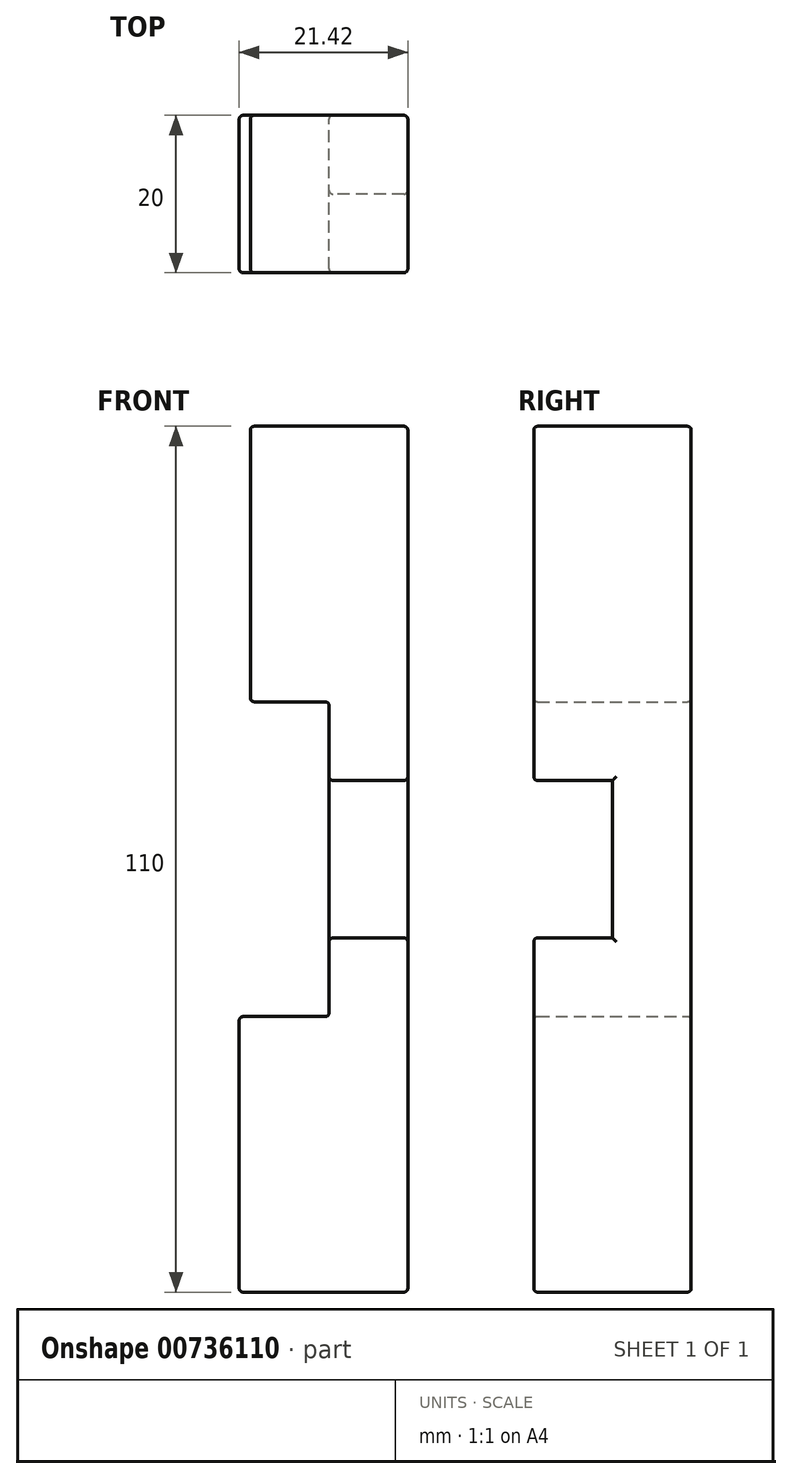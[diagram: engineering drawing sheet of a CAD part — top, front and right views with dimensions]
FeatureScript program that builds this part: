
annotation { "Feature Type Name" : "Feature", "Feature Type Description" : "" }
export const myFeature = defineFeature(function(context is Context, id is Id, definition is map)
    precondition{}
    {
        {
            var Q0;
            Q0=qCreatedBy(makeId("Front.planeOp"),FACE);
            var sketch = newSketch(context, id + "F0", { "sketchPlane" : qUnion([Q0])});
            skLineSegment(sketch, "E0", {"start": v(-10, 21.51) * mm, "end": v(-10, 56.51) * mm});
            skLineSegment(sketch, "E1", {"start": v(-10, 56.51) * mm, "end": v(10, 56.51) * mm});
            skLineSegment(sketch, "E2", {"start": v(10, 56.51) * mm, "end": v(10, -53.49) * mm});
            skLineSegment(sketch, "E3", {"start": v(10, -53.49) * mm, "end": v(-11.42, -53.49) * mm});
            skLineSegment(sketch, "E4", {"start": v(-11.42, -53.49) * mm, "end": v(-11.42, -18.49) * mm});
            skLineSegment(sketch, "E5", {"start": v(-11.42, -18.49) * mm, "end": v(0, -18.49) * mm});
            skLineSegment(sketch, "E6", {"start": v(0, -18.49) * mm, "end": v(0, 21.51) * mm});
            skLineSegment(sketch, "E7", {"start": v(0, 21.51) * mm, "end": v(-10, 21.51) * mm});
            skLineSegment(sketch, "E8", {"start": v(0, 11.51) * mm, "end": v(10, 11.51) * mm});
            skLineSegment(sketch, "E9", {"start": v(0, -8.49) * mm, "end": v(10, -8.49) * mm});
            skSolve(sketch);
        }
        {
            var Q0;
            Q0=makeQuery(id+"F0.imprint","IMPRINT",FACE,{"disambiguationData":[TD([[makeQuery(id+"F0.imprint","IMPRINT",EDGE,{"derivedFrom":sQuery(id+"F0.wireOp",EDGE,"E0")}),-1.0]])]});
            var Q1;
            {var subQ1=sQuery(id+"F0.wireOp",EDGE,"E3");Q1=makeQuery(id+"F0.imprint","IMPRINT",FACE,{"disambiguationData":[TD([[makeQuery(id+"F0.imprint","IMPRINT",EDGE,{"derivedFrom":subQ1}),-1.0]])]});}
            var Q2;
            {var subQ0=sQuery(id+"F0.wireOp",EDGE,"E8");Q2=makeQuery(id+"F0.imprint","IMPRINT",FACE,{"disambiguationData":[TD([[makeQuery(id+"F0.imprint","IMPRINT",EDGE,{"derivedFrom":subQ0}),-1.0]])]});}
            extrude(context, id + "F1", {"entities" : qUnion([Q0, Q1, Q2]), "depth" : 10 * mm, "offsetDistance" : 25 * mm});
        }
        {
            var Q0;
            Q0=makeQuery(id+"F0.imprint","IMPRINT",FACE,{"disambiguationData":[TD([[makeQuery(id+"F0.imprint","IMPRINT",EDGE,{"derivedFrom":sQuery(id+"F0.wireOp",EDGE,"E0")}),-1.0]])]});
            var Q1;
            {var subQ1=sQuery(id+"F0.wireOp",EDGE,"E3");Q1=makeQuery(id+"F0.imprint","IMPRINT",FACE,{"disambiguationData":[TD([[makeQuery(id+"F0.imprint","IMPRINT",EDGE,{"derivedFrom":subQ1}),-1.0]])]});}
            extrude(context, id + "F2", {"entities" : qUnion([Q0, Q1]), "operationType" : NewBodyOperationType.ADD, "depth" : 20 * mm, "offsetDistance" : 25 * mm});
        }
        {
            var Q0;
            Q0=makeQuery(id+"F2.opExtrude","CAP_FACE",FACE,{"disambiguationData":[OSD([sQuery(id+"F0.wireOp",EDGE,"E0"),sQuery(id+"F0.wireOp",EDGE,"E1"),sQuery(id+"F0.wireOp",EDGE,"E2"),sQuery(id+"F0.wireOp",EDGE,"E6"),sQuery(id+"F0.wireOp",EDGE,"E7"),sQuery(id+"F0.wireOp",EDGE,"E8")])],"isStart":false});
            var Q1;
            Q1=makeQuery(id+"F2.opExtrude","CAP_FACE",FACE,{"disambiguationData":[OSD([sQuery(id+"F0.wireOp",EDGE,"E2"),sQuery(id+"F0.wireOp",EDGE,"E3"),sQuery(id+"F0.wireOp",EDGE,"E4"),sQuery(id+"F0.wireOp",EDGE,"E5"),sQuery(id+"F0.wireOp",EDGE,"E6"),sQuery(id+"F0.wireOp",EDGE,"E9")])],"isStart":false});
            var Q2;
            {var subQ0=sQuery(id+"F0.wireOp",EDGE,"E0");Q2=makeQuery(id+"F2.boolean.opBoolean","MERGE",FACE,{"derivedFrom":[makeQuery(id+"F1.opExtrude","SWEPT_FACE",FACE,{"disambiguationData":[OSD([subQ0])]}),makeQuery(id+"F2.opExtrude","SWEPT_FACE",FACE,{"disambiguationData":[OSD([subQ0])]})]});}
            var Q3;
            {var subQ0=sQuery(id+"F0.wireOp",EDGE,"E4");Q3=makeQuery(id+"F2.boolean.opBoolean","MERGE",FACE,{"derivedFrom":[makeQuery(id+"F1.opExtrude","SWEPT_FACE",FACE,{"disambiguationData":[OSD([subQ0])]}),makeQuery(id+"F2.opExtrude","SWEPT_FACE",FACE,{"disambiguationData":[OSD([subQ0])]})]});}
            var Q4;
            {var subQ0=sQuery(id+"F0.wireOp",EDGE,"E6");Q4=makeQuery(id+"F2.boolean.opBoolean","MERGE",FACE,{"derivedFrom":[makeQuery(id+"F1.opExtrude","SWEPT_FACE",FACE,{"disambiguationData":[OSD([subQ0])]}),makeQuery(id+"F2.opExtrude","SWEPT_FACE",FACE,{"disambiguationData":[OSD([subQ0]),TDD([makeQuery(id+"F0.imprint","IMPRINT",EDGE,{"disambiguationData":[TD([[makeQuery(id+"F0.imprint","INTERSECT",VERTEX,{"derivedFrom":[sQuery(id+"F0.wireOp",EDGE,"E5"),subQ0]}),-1.0]])],"derivedFrom":subQ0})])]}),makeQuery(id+"F2.opExtrude","SWEPT_FACE",FACE,{"disambiguationData":[OSD([subQ0]),TDD([makeQuery(id+"F0.imprint","IMPRINT",EDGE,{"disambiguationData":[TD([[makeQuery(id+"F0.imprint","INTERSECT",VERTEX,{"derivedFrom":[subQ0,sQuery(id+"F0.wireOp",EDGE,"E7")]}),1.0]])],"derivedFrom":subQ0})])]})]});}
            var Q5;
            Q5=makeQuery(id+"F1.opExtrude","CAP_FACE",FACE,{"disambiguationData":[OSD([sQuery(id+"F0.wireOp",EDGE,"E0"),sQuery(id+"F0.wireOp",EDGE,"E1"),sQuery(id+"F0.wireOp",EDGE,"E2"),sQuery(id+"F0.wireOp",EDGE,"E3"),sQuery(id+"F0.wireOp",EDGE,"E4"),sQuery(id+"F0.wireOp",EDGE,"E5"),sQuery(id+"F0.wireOp",EDGE,"E6"),sQuery(id+"F0.wireOp",EDGE,"E7")])],"isStart":true});
            var Q6;
            {var subQ0=sQuery(id+"F0.wireOp",EDGE,"E2");Q6=makeQuery(id+"F2.boolean.opBoolean","MERGE",FACE,{"derivedFrom":[makeQuery(id+"F1.opExtrude","SWEPT_FACE",FACE,{"disambiguationData":[OSD([subQ0])]}),makeQuery(id+"F2.opExtrude","SWEPT_FACE",FACE,{"disambiguationData":[OSD([subQ0]),TDD([makeQuery(id+"F0.imprint","IMPRINT",EDGE,{"disambiguationData":[TD([[makeQuery(id+"F0.imprint","INTERSECT",VERTEX,{"derivedFrom":[sQuery(id+"F0.wireOp",EDGE,"E1"),subQ0]}),-1.0]])],"derivedFrom":subQ0})])]}),makeQuery(id+"F2.opExtrude","SWEPT_FACE",FACE,{"disambiguationData":[OSD([subQ0]),TDD([makeQuery(id+"F0.imprint","IMPRINT",EDGE,{"disambiguationData":[TD([[makeQuery(id+"F0.imprint","INTERSECT",VERTEX,{"derivedFrom":[subQ0,sQuery(id+"F0.wireOp",EDGE,"E3")]}),1.0]])],"derivedFrom":subQ0})])]})]});}
            fillet(context, id + "F3", {"entities" : qUnion([Q0, Q1, Q2, Q3, Q4, Q5, Q6]), "radius" : 0.5 * mm, "tangentPropagation" : true, "allowEdgeOverflow" : false});
        }
    });
